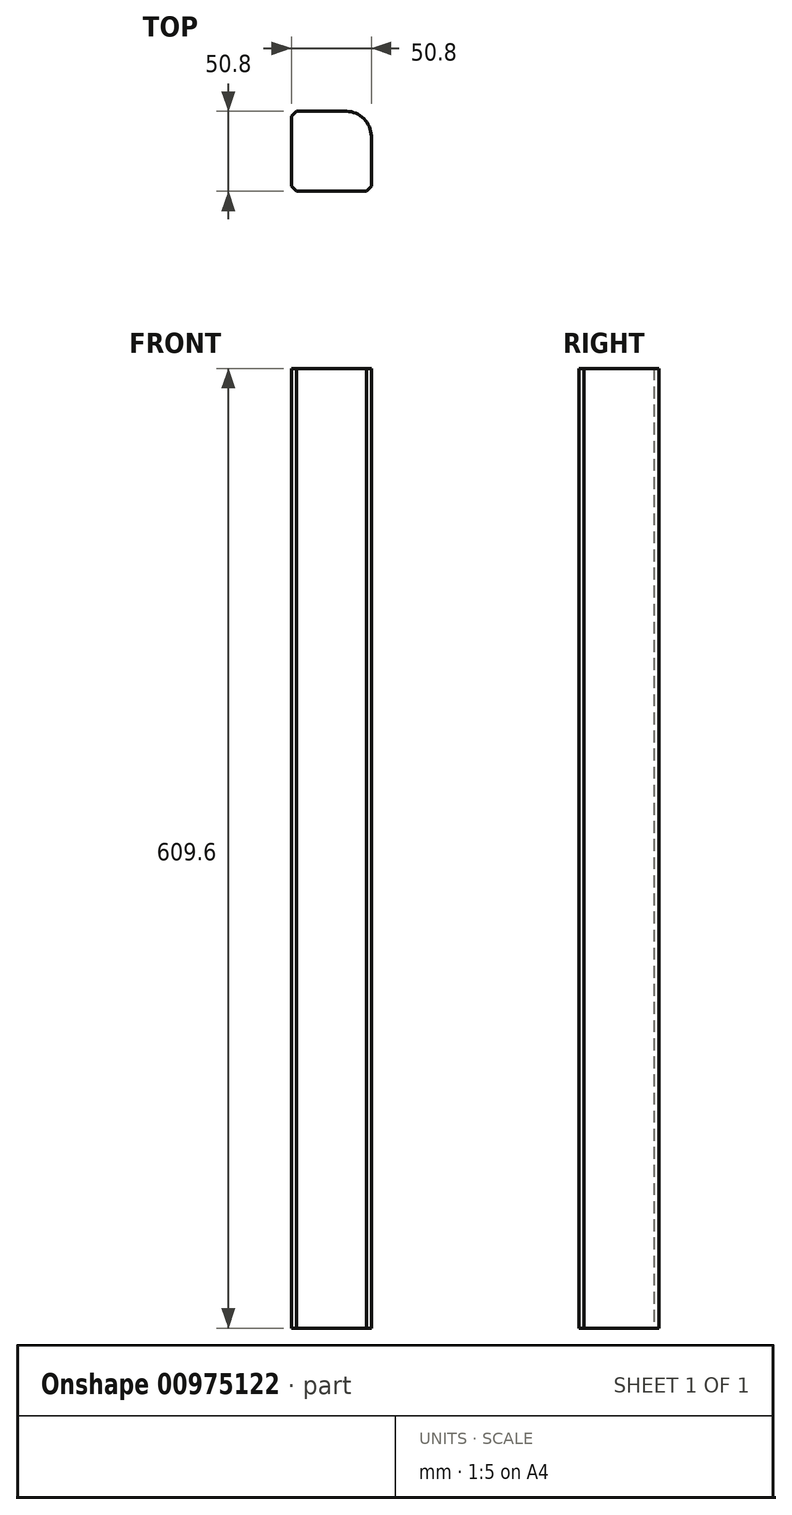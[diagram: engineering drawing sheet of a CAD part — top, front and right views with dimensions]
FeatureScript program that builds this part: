
annotation { "Feature Type Name" : "Feature", "Feature Type Description" : "" }
export const myFeature = defineFeature(function(context is Context, id is Id, definition is map)
    precondition{}
    {
        {
            var Q0;
            Q0=qCreatedBy(makeId("Top.planeOp"),FACE);
            var sketch = newSketch(context, id + "F0", { "sketchPlane" : qUnion([Q0])});
            skLineSegment(sketch, "E0.bottom", {"start": v(0, 0) * mm, "end": v(50.8, 0) * mm});
            skLineSegment(sketch, "E0.top", {"start": v(0, -50.8) * mm, "end": v(50.8, -50.8) * mm});
            skLineSegment(sketch, "E0.left", {"start": v(0, 0) * mm, "end": v(0, -50.8) * mm});
            skLineSegment(sketch, "E0.right", {"start": v(50.8, 0) * mm, "end": v(50.8, -50.8) * mm});
            skSolve(sketch);
        }
        {
            var Q0;
            Q0 = qSketchRegion(id + "F0", true);
            extrude(context, id + "F1", {"entities" : qUnion([Q0]), "depth" : 609.6 * mm, "offsetDistance" : 25.4 * mm});
        }
        {
            var Q0;
            Q0=makeQuery(id+"F1.opExtrude","SWEPT_EDGE",EDGE,{"disambiguationData":[OSD([sQuery(id+"F0.wireOp",EDGE,"E0.bottom"),sQuery(id+"F0.wireOp",EDGE,"E0.right")])]});
            fillet(context, id + "F2", {"entities" : qUnion([Q0]), "radius" : 15.88 * mm, "tangentPropagation" : true, "allowEdgeOverflow" : false});
        }
        {
            var Q0;
            Q0=makeQuery(id+"F1.opExtrude","SWEPT_EDGE",EDGE,{"disambiguationData":[OSD([sQuery(id+"F0.wireOp",EDGE,"E0.bottom"),sQuery(id+"F0.wireOp",EDGE,"E0.left")])]});
            var Q1;
            Q1=makeQuery(id+"F1.opExtrude","SWEPT_EDGE",EDGE,{"disambiguationData":[OSD([sQuery(id+"F0.wireOp",EDGE,"E0.top"),sQuery(id+"F0.wireOp",EDGE,"E0.left")])]});
            var Q2;
            Q2=makeQuery(id+"F1.opExtrude","SWEPT_EDGE",EDGE,{"disambiguationData":[OSD([sQuery(id+"F0.wireOp",EDGE,"E0.top"),sQuery(id+"F0.wireOp",EDGE,"E0.right")])]});
            chamfer(context, id + "F3", {"entities" : qUnion([Q0, Q1, Q2]), "width" : 3.17 * mm, "tangentPropagation" : true});
        }
    });
